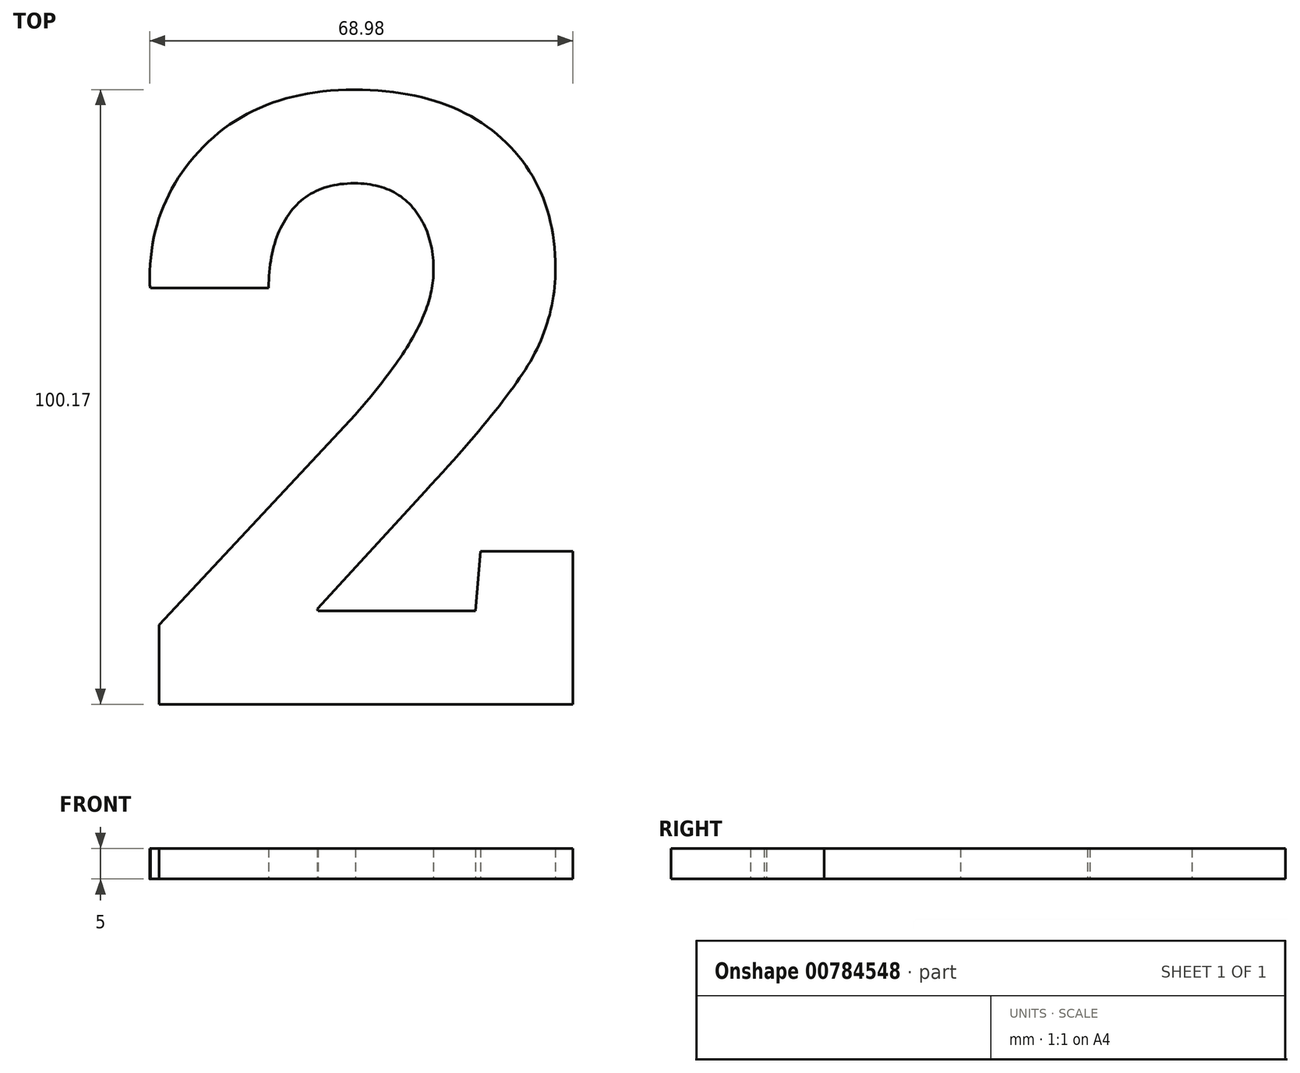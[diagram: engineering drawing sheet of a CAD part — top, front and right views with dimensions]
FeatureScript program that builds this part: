
annotation { "Feature Type Name" : "Feature", "Feature Type Description" : "" }
export const myFeature = defineFeature(function(context is Context, id is Id, definition is map)
    precondition{}
    {
        {
            var Q0;
            Q0=qCreatedBy(makeId("Top.planeOp"),FACE);
            var sketch = newSketch(context, id + "F0", { "sketchPlane" : qUnion([Q0])});
            skText(sketch, "E0", { "text": "2", "fontName": "RobotoSlab-Bold.ttf"});
            const initialGuessF0  = {"E0": [0, 0, 1, 0, 0.1]};
            skSetInitialGuess(sketch, initialGuessF0);
            skSolve(sketch);
        }
        {
            var Q0;
            Q0 = qSketchRegion(id + "F0", true);
            extrude(context, id + "F1", {"entities" : qUnion([Q0]), "depth" : 5 * mm, "offsetDistance" : 25 * mm});
        }
    });
